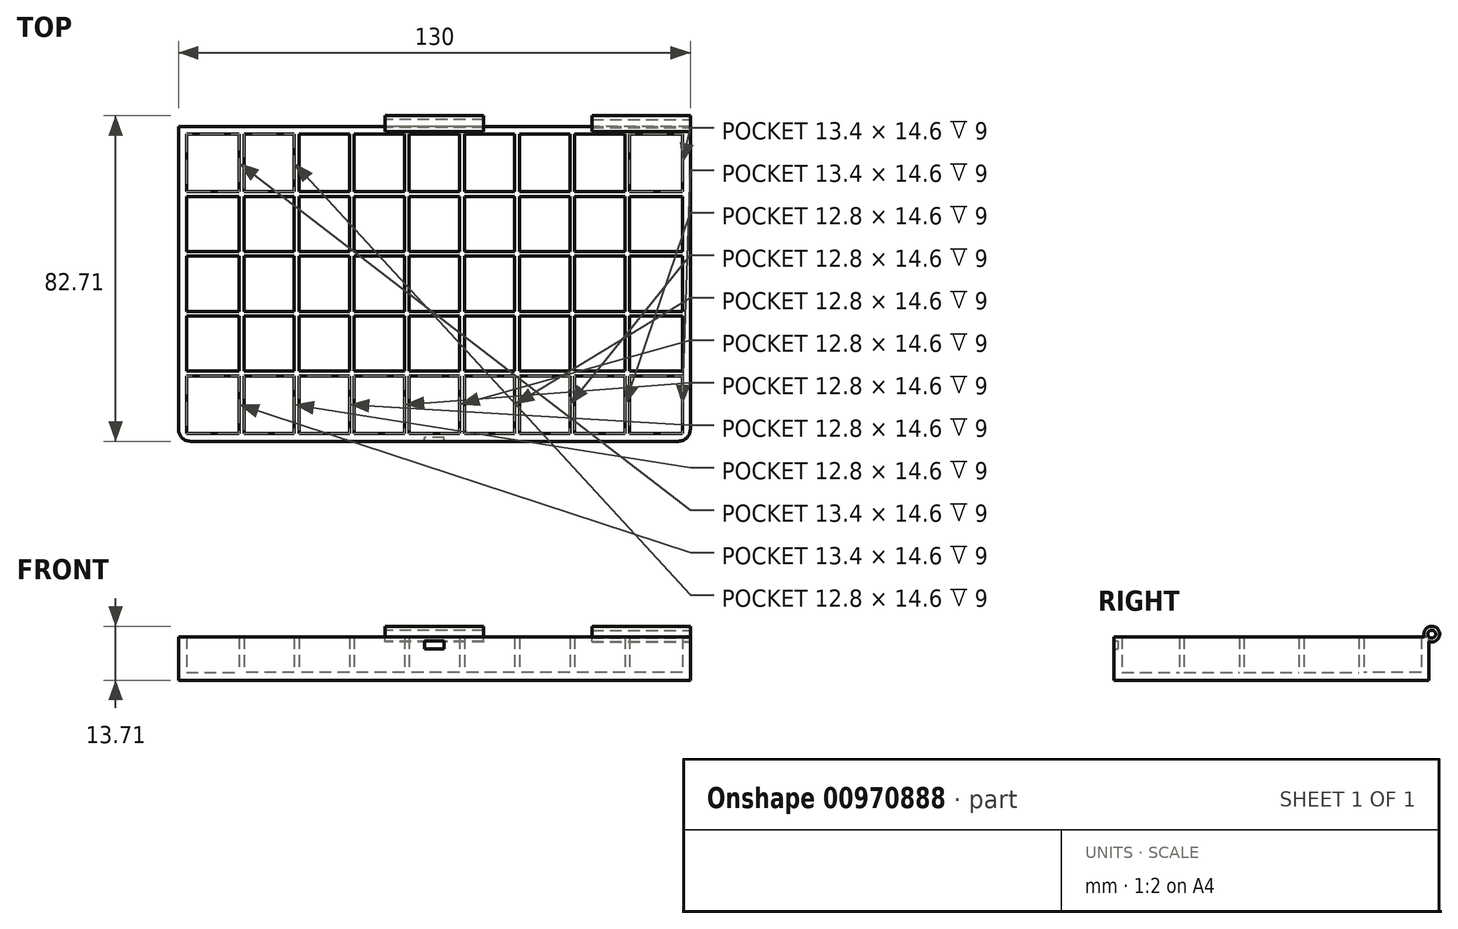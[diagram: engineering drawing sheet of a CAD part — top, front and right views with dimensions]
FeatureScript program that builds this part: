
annotation { "Feature Type Name" : "Feature", "Feature Type Description" : "" }
export const myFeature = defineFeature(function(context is Context, id is Id, definition is map)
    precondition{}
    {
        {
            var Q0;
            Q0=qCreatedBy(makeId("Top.planeOp"),FACE);
            var sketch = newSketch(context, id + "F0", { "sketchPlane" : qUnion([Q0])});
            skLineSegment(sketch, "E0.bottom", {"start": v(0, 0) * mm, "end": v(-130, 0) * mm});
            skLineSegment(sketch, "E0.top", {"start": v(0, 80) * mm, "end": v(-130, 80) * mm});
            skLineSegment(sketch, "E0.left", {"start": v(0, 0) * mm, "end": v(0, 80) * mm});
            skLineSegment(sketch, "E0.right", {"start": v(-130, 0) * mm, "end": v(-130, 80) * mm});
            skSolve(sketch);
        }
        {
            var Q0;
            Q0=makeQuery(id+"F0.imprint","IMPRINT",FACE,{"disambiguationData":[TD([[makeQuery(id+"F0.imprint","IMPRINT",EDGE,{"derivedFrom":sQuery(id+"F0.wireOp",EDGE,"E0.bottom")}),-1.0]])]});
            extrude(context, id + "F1", {"entities" : qUnion([Q0]), "depth" : 11 * mm, "offsetDistance" : 25 * mm});
        }
        {
            var Q0;
            Q0=makeQuery(id+"F1.opExtrude","CAP_FACE",FACE,{"disambiguationData":[OSD([sQuery(id+"F0.wireOp",EDGE,"E0.bottom"),sQuery(id+"F0.wireOp",EDGE,"E0.top"),sQuery(id+"F0.wireOp",EDGE,"E0.left"),sQuery(id+"F0.wireOp",EDGE,"E0.right")])],"isStart":false});
            shell(context, id + "F2", {"entities" : qUnion([Q0]), "thickness" : 2 * mm});
        }
        {
            var Q0;
            Q0=makeQuery(id+"F2.opShell","OFFSET_FACE",FACE,{"disambiguationData":[OSD([sQuery(id+"F0.wireOp",EDGE,"E0.bottom"),sQuery(id+"F0.wireOp",EDGE,"E0.top"),sQuery(id+"F0.wireOp",EDGE,"E0.left"),sQuery(id+"F0.wireOp",EDGE,"E0.right")])]});
            var sketch = newSketch(context, id + "F3", { "sketchPlane" : qUnion([Q0])});
            skLineSegment(sketch, "E1", {"start": v(-128, 62.8) * mm, "end": v(-2, 62.8) * mm, "construction": true});
            skLineSegment(sketch, "E2.0.1.0", {"start": v(-128, 47.6) * mm, "end": v(-2, 47.6) * mm, "construction": true});
            skLineSegment(sketch, "E2.0.2.0", {"start": v(-128, 32.4) * mm, "end": v(-2, 32.4) * mm, "construction": true});
            skLineSegment(sketch, "E2.0.3.0", {"start": v(-128, 17.2) * mm, "end": v(-2, 17.2) * mm, "construction": true});
            skLineSegment(sketch, "E2.direction1", {"start": v(-128, 62.8) * mm, "end": v(-103, 62.8) * mm, "construction": true});
            skLineSegment(sketch, "E2.direction2", {"start": v(-128, 62.8) * mm, "end": v(-128, 47.6) * mm, "construction": true});
            skLineSegment(sketch, "E3", {"start": v(-115.48, 78) * mm, "end": v(-115.48, 62.8) * mm, "construction": true});
            skLineSegment(sketch, "E4", {"start": v(-116.19, 17.2) * mm, "end": v(-116.19, 2) * mm, "construction": true});
            skLineSegment(sketch, "E5", {"start": v(-115.48, 62.8) * mm, "end": v(-115.48, 47.6) * mm, "construction": true});
            skLineSegment(sketch, "E6", {"start": v(-114, 78) * mm, "end": v(-114, 2) * mm, "construction": true});
            skLineSegment(sketch, "E7.1.0.0", {"start": v(-100, 78) * mm, "end": v(-100, 2) * mm, "construction": true});
            skLineSegment(sketch, "E7.2.0.0", {"start": v(-86, 78) * mm, "end": v(-86, 2) * mm, "construction": true});
            skLineSegment(sketch, "E7.3.0.0", {"start": v(-72, 78) * mm, "end": v(-72, 2) * mm, "construction": true});
            skLineSegment(sketch, "E7.4.0.0", {"start": v(-58, 78) * mm, "end": v(-58, 2) * mm, "construction": true});
            skLineSegment(sketch, "E7.5.0.0", {"start": v(-44, 78) * mm, "end": v(-44, 2) * mm, "construction": true});
            skLineSegment(sketch, "E7.6.0.0", {"start": v(-30, 78) * mm, "end": v(-30, 2) * mm, "construction": true});
            skLineSegment(sketch, "E7.7.0.0", {"start": v(-16, 78) * mm, "end": v(-16, 2) * mm, "construction": true});
            skLineSegment(sketch, "E7.direction1", {"start": v(-114, 2) * mm, "end": v(-100, 2) * mm, "construction": true});
            skLineSegment(sketch, "E8", {"start": v(-114, 25.91) * mm, "end": v(-128, 25.91) * mm, "construction": true});
            skLineSegment(sketch, "E9", {"start": v(-16, 25.73) * mm, "end": v(-2, 25.73) * mm, "construction": true});
            skLineSegment(sketch, "E10", {"start": v(-114, 25.91) * mm, "end": v(-100, 25.91) * mm, "construction": true});
            skArc(sketch, "E11.0.startCap", {"start": v(-128, 62.2) * mm, "mid": v(-128.6, 62.8) * mm, "end": v(-128, 63.4) * mm});
            skArc(sketch, "E11.0.endCap", {"start": v(-2, 63.4) * mm, "mid": v(-1.4, 62.8) * mm, "end": v(-2, 62.2) * mm});
            skLineSegment(sketch, "E11.0.left", {"start": v(-128, 63.4) * mm, "end": v(-2, 63.4) * mm});
            skLineSegment(sketch, "E11.0.right", {"start": v(-128, 62.2) * mm, "end": v(-2, 62.2) * mm});
            skArc(sketch, "E11.1.startCap", {"start": v(-30.6, 78) * mm, "mid": v(-30, 78.6) * mm, "end": v(-29.4, 78) * mm});
            skArc(sketch, "E11.1.endCap", {"start": v(-29.4, 2) * mm, "mid": v(-30, 1.4) * mm, "end": v(-30.6, 2) * mm});
            skLineSegment(sketch, "E11.1.left", {"start": v(-29.4, 78) * mm, "end": v(-29.4, 2) * mm});
            skLineSegment(sketch, "E11.1.right", {"start": v(-30.6, 78) * mm, "end": v(-30.6, 2) * mm});
            skArc(sketch, "E11.2.startCap", {"start": v(-86.6, 78) * mm, "mid": v(-86, 78.6) * mm, "end": v(-85.4, 78) * mm});
            skArc(sketch, "E11.2.endCap", {"start": v(-85.4, 2) * mm, "mid": v(-86, 1.4) * mm, "end": v(-86.6, 2) * mm});
            skLineSegment(sketch, "E11.2.left", {"start": v(-85.4, 78) * mm, "end": v(-85.4, 2) * mm});
            skLineSegment(sketch, "E11.2.right", {"start": v(-86.6, 78) * mm, "end": v(-86.6, 2) * mm});
            skArc(sketch, "E11.3.startCap", {"start": v(-100.6, 78) * mm, "mid": v(-100, 78.6) * mm, "end": v(-99.4, 78) * mm});
            skArc(sketch, "E11.3.endCap", {"start": v(-99.4, 2) * mm, "mid": v(-100, 1.4) * mm, "end": v(-100.6, 2) * mm});
            skLineSegment(sketch, "E11.3.left", {"start": v(-99.4, 78) * mm, "end": v(-99.4, 2) * mm});
            skLineSegment(sketch, "E11.3.right", {"start": v(-100.6, 78) * mm, "end": v(-100.6, 2) * mm});
            skArc(sketch, "E11.4.startCap", {"start": v(-44.6, 78) * mm, "mid": v(-44, 78.6) * mm, "end": v(-43.4, 78) * mm});
            skArc(sketch, "E11.4.endCap", {"start": v(-43.4, 2) * mm, "mid": v(-44, 1.4) * mm, "end": v(-44.6, 2) * mm});
            skLineSegment(sketch, "E11.4.left", {"start": v(-43.4, 78) * mm, "end": v(-43.4, 2) * mm});
            skLineSegment(sketch, "E11.4.right", {"start": v(-44.6, 78) * mm, "end": v(-44.6, 2) * mm});
            skArc(sketch, "E11.5.startCap", {"start": v(-128, 16.6) * mm, "mid": v(-128.6, 17.2) * mm, "end": v(-128, 17.8) * mm});
            skArc(sketch, "E11.5.endCap", {"start": v(-2, 17.8) * mm, "mid": v(-1.4, 17.2) * mm, "end": v(-2, 16.6) * mm});
            skLineSegment(sketch, "E11.5.left", {"start": v(-128, 17.8) * mm, "end": v(-2, 17.8) * mm});
            skLineSegment(sketch, "E11.5.right", {"start": v(-128, 16.6) * mm, "end": v(-2, 16.6) * mm});
            skArc(sketch, "E11.6.startCap", {"start": v(-128, 47) * mm, "mid": v(-128.6, 47.6) * mm, "end": v(-128, 48.2) * mm});
            skArc(sketch, "E11.6.endCap", {"start": v(-2, 48.2) * mm, "mid": v(-1.4, 47.6) * mm, "end": v(-2, 47) * mm});
            skLineSegment(sketch, "E11.6.left", {"start": v(-128, 48.2) * mm, "end": v(-2, 48.2) * mm});
            skLineSegment(sketch, "E11.6.right", {"start": v(-128, 47) * mm, "end": v(-2, 47) * mm});
            skArc(sketch, "E11.7.startCap", {"start": v(-114.6, 78) * mm, "mid": v(-114, 78.6) * mm, "end": v(-113.4, 78) * mm});
            skArc(sketch, "E11.7.endCap", {"start": v(-113.4, 2) * mm, "mid": v(-114, 1.4) * mm, "end": v(-114.6, 2) * mm});
            skLineSegment(sketch, "E11.7.left", {"start": v(-113.4, 78) * mm, "end": v(-113.4, 2) * mm});
            skLineSegment(sketch, "E11.7.right", {"start": v(-114.6, 78) * mm, "end": v(-114.6, 2) * mm});
            skArc(sketch, "E11.8.startCap", {"start": v(-16.6, 78) * mm, "mid": v(-16, 78.6) * mm, "end": v(-15.4, 78) * mm});
            skArc(sketch, "E11.8.endCap", {"start": v(-15.4, 2) * mm, "mid": v(-16, 1.4) * mm, "end": v(-16.6, 2) * mm});
            skLineSegment(sketch, "E11.8.left", {"start": v(-15.4, 78) * mm, "end": v(-15.4, 2) * mm});
            skLineSegment(sketch, "E11.8.right", {"start": v(-16.6, 78) * mm, "end": v(-16.6, 2) * mm});
            skArc(sketch, "E11.9.startCap", {"start": v(-58.6, 78) * mm, "mid": v(-58, 78.6) * mm, "end": v(-57.4, 78) * mm});
            skArc(sketch, "E11.9.endCap", {"start": v(-57.4, 2) * mm, "mid": v(-58, 1.4) * mm, "end": v(-58.6, 2) * mm});
            skLineSegment(sketch, "E11.9.left", {"start": v(-57.4, 78) * mm, "end": v(-57.4, 2) * mm});
            skLineSegment(sketch, "E11.9.right", {"start": v(-58.6, 78) * mm, "end": v(-58.6, 2) * mm});
            skArc(sketch, "E11.10.startCap", {"start": v(-72.6, 78) * mm, "mid": v(-72, 78.6) * mm, "end": v(-71.4, 78) * mm});
            skArc(sketch, "E11.10.endCap", {"start": v(-71.4, 2) * mm, "mid": v(-72, 1.4) * mm, "end": v(-72.6, 2) * mm});
            skLineSegment(sketch, "E11.10.left", {"start": v(-71.4, 78) * mm, "end": v(-71.4, 2) * mm});
            skLineSegment(sketch, "E11.10.right", {"start": v(-72.6, 78) * mm, "end": v(-72.6, 2) * mm});
            skArc(sketch, "E11.11.startCap", {"start": v(-128, 31.8) * mm, "mid": v(-128.6, 32.4) * mm, "end": v(-128, 33) * mm});
            skArc(sketch, "E11.11.endCap", {"start": v(-2, 33) * mm, "mid": v(-1.4, 32.4) * mm, "end": v(-2, 31.8) * mm});
            skLineSegment(sketch, "E11.11.left", {"start": v(-128, 33) * mm, "end": v(-2, 33) * mm});
            skLineSegment(sketch, "E11.11.right", {"start": v(-128, 31.8) * mm, "end": v(-2, 31.8) * mm});
            skSolve(sketch);
        }
        {
            var Q0;
            {var subQ0=sQuery(id+"F3.wireOp",EDGE,"E11.7.right");var subQ1=sQuery(id+"F3.wireOp",EDGE,"E11.0.left");var subQ2=makeQuery(id+"F3.imprint","INTERSECT",VERTEX,{"derivedFrom":[subQ1,subQ0]});Q0=makeQuery(id+"F3.imprint","IMPRINT",FACE,{"disambiguationData":[TD([[makeQuery(id+"F3.imprint","IMPRINT",EDGE,{"disambiguationData":[TD([[subQ2,-1.0]])],"derivedFrom":subQ1}),-1.0]])]});}
            var Q1;
            {var subQ0=sQuery(id+"F3.wireOp",EDGE,"E11.7.left");var subQ1=sQuery(id+"F3.wireOp",EDGE,"E11.0.left");var subQ2=makeQuery(id+"F3.imprint","INTERSECT",VERTEX,{"derivedFrom":[subQ1,subQ0]});Q1=makeQuery(id+"F3.imprint","IMPRINT",FACE,{"disambiguationData":[TD([[makeQuery(id+"F3.imprint","IMPRINT",EDGE,{"disambiguationData":[TD([[subQ2,-1.0]])],"derivedFrom":subQ1}),-1.0]])]});}
            var Q2;
            {var subQ0=sQuery(id+"F3.wireOp",EDGE,"E11.3.right");var subQ1=sQuery(id+"F3.wireOp",EDGE,"E11.0.left");var subQ2=makeQuery(id+"F3.imprint","INTERSECT",VERTEX,{"derivedFrom":[subQ1,subQ0]});Q2=makeQuery(id+"F3.imprint","IMPRINT",FACE,{"disambiguationData":[TD([[makeQuery(id+"F3.imprint","IMPRINT",EDGE,{"disambiguationData":[TD([[subQ2,-1.0]])],"derivedFrom":subQ1}),-1.0]])]});}
            var Q3;
            {var subQ0=sQuery(id+"F3.wireOp",EDGE,"E11.3.left");var subQ1=sQuery(id+"F3.wireOp",EDGE,"E11.0.left");var subQ2=makeQuery(id+"F3.imprint","INTERSECT",VERTEX,{"derivedFrom":[subQ1,subQ0]});Q3=makeQuery(id+"F3.imprint","IMPRINT",FACE,{"disambiguationData":[TD([[makeQuery(id+"F3.imprint","IMPRINT",EDGE,{"disambiguationData":[TD([[subQ2,-1.0]])],"derivedFrom":subQ1}),-1.0]])]});}
            var Q4;
            {var subQ0=sQuery(id+"F3.wireOp",EDGE,"E11.2.right");var subQ1=sQuery(id+"F3.wireOp",EDGE,"E11.0.left");var subQ2=makeQuery(id+"F3.imprint","INTERSECT",VERTEX,{"derivedFrom":[subQ1,subQ0]});Q4=makeQuery(id+"F3.imprint","IMPRINT",FACE,{"disambiguationData":[TD([[makeQuery(id+"F3.imprint","IMPRINT",EDGE,{"disambiguationData":[TD([[subQ2,-1.0]])],"derivedFrom":subQ1}),-1.0]])]});}
            var Q5;
            {var subQ0=sQuery(id+"F3.wireOp",EDGE,"E11.2.left");var subQ1=sQuery(id+"F3.wireOp",EDGE,"E11.0.left");var subQ2=makeQuery(id+"F3.imprint","INTERSECT",VERTEX,{"derivedFrom":[subQ1,subQ0]});Q5=makeQuery(id+"F3.imprint","IMPRINT",FACE,{"disambiguationData":[TD([[makeQuery(id+"F3.imprint","IMPRINT",EDGE,{"disambiguationData":[TD([[subQ2,-1.0]])],"derivedFrom":subQ1}),-1.0]])]});}
            var Q6;
            {var subQ0=sQuery(id+"F3.wireOp",EDGE,"E11.10.right");var subQ1=sQuery(id+"F3.wireOp",EDGE,"E11.0.left");var subQ2=makeQuery(id+"F3.imprint","INTERSECT",VERTEX,{"derivedFrom":[subQ1,subQ0]});Q6=makeQuery(id+"F3.imprint","IMPRINT",FACE,{"disambiguationData":[TD([[makeQuery(id+"F3.imprint","IMPRINT",EDGE,{"disambiguationData":[TD([[subQ2,-1.0]])],"derivedFrom":subQ1}),-1.0]])]});}
            var Q7;
            {var subQ0=sQuery(id+"F3.wireOp",EDGE,"E11.10.left");var subQ1=sQuery(id+"F3.wireOp",EDGE,"E11.0.left");var subQ2=makeQuery(id+"F3.imprint","INTERSECT",VERTEX,{"derivedFrom":[subQ1,subQ0]});Q7=makeQuery(id+"F3.imprint","IMPRINT",FACE,{"disambiguationData":[TD([[makeQuery(id+"F3.imprint","IMPRINT",EDGE,{"disambiguationData":[TD([[subQ2,-1.0]])],"derivedFrom":subQ1}),-1.0]])]});}
            var Q8;
            {var subQ0=sQuery(id+"F3.wireOp",EDGE,"E11.9.right");var subQ1=sQuery(id+"F3.wireOp",EDGE,"E11.0.left");var subQ2=makeQuery(id+"F3.imprint","INTERSECT",VERTEX,{"derivedFrom":[subQ1,subQ0]});Q8=makeQuery(id+"F3.imprint","IMPRINT",FACE,{"disambiguationData":[TD([[makeQuery(id+"F3.imprint","IMPRINT",EDGE,{"disambiguationData":[TD([[subQ2,-1.0]])],"derivedFrom":subQ1}),-1.0]])]});}
            var Q9;
            {var subQ0=sQuery(id+"F3.wireOp",EDGE,"E11.9.left");var subQ1=sQuery(id+"F3.wireOp",EDGE,"E11.0.left");var subQ2=makeQuery(id+"F3.imprint","INTERSECT",VERTEX,{"derivedFrom":[subQ1,subQ0]});Q9=makeQuery(id+"F3.imprint","IMPRINT",FACE,{"disambiguationData":[TD([[makeQuery(id+"F3.imprint","IMPRINT",EDGE,{"disambiguationData":[TD([[subQ2,-1.0]])],"derivedFrom":subQ1}),-1.0]])]});}
            var Q10;
            {var subQ0=sQuery(id+"F3.wireOp",EDGE,"E11.4.right");var subQ1=sQuery(id+"F3.wireOp",EDGE,"E11.0.left");var subQ2=makeQuery(id+"F3.imprint","INTERSECT",VERTEX,{"derivedFrom":[subQ1,subQ0]});Q10=makeQuery(id+"F3.imprint","IMPRINT",FACE,{"disambiguationData":[TD([[makeQuery(id+"F3.imprint","IMPRINT",EDGE,{"disambiguationData":[TD([[subQ2,-1.0]])],"derivedFrom":subQ1}),-1.0]])]});}
            var Q11;
            {var subQ0=sQuery(id+"F3.wireOp",EDGE,"E11.4.left");var subQ1=sQuery(id+"F3.wireOp",EDGE,"E11.0.left");var subQ2=makeQuery(id+"F3.imprint","INTERSECT",VERTEX,{"derivedFrom":[subQ1,subQ0]});Q11=makeQuery(id+"F3.imprint","IMPRINT",FACE,{"disambiguationData":[TD([[makeQuery(id+"F3.imprint","IMPRINT",EDGE,{"disambiguationData":[TD([[subQ2,-1.0]])],"derivedFrom":subQ1}),-1.0]])]});}
            var Q12;
            {var subQ0=sQuery(id+"F3.wireOp",EDGE,"E11.1.right");var subQ1=sQuery(id+"F3.wireOp",EDGE,"E11.0.left");var subQ2=makeQuery(id+"F3.imprint","INTERSECT",VERTEX,{"derivedFrom":[subQ1,subQ0]});Q12=makeQuery(id+"F3.imprint","IMPRINT",FACE,{"disambiguationData":[TD([[makeQuery(id+"F3.imprint","IMPRINT",EDGE,{"disambiguationData":[TD([[subQ2,-1.0]])],"derivedFrom":subQ1}),-1.0]])]});}
            var Q13;
            {var subQ0=sQuery(id+"F3.wireOp",EDGE,"E11.1.left");var subQ1=sQuery(id+"F3.wireOp",EDGE,"E11.0.left");var subQ2=makeQuery(id+"F3.imprint","INTERSECT",VERTEX,{"derivedFrom":[subQ1,subQ0]});Q13=makeQuery(id+"F3.imprint","IMPRINT",FACE,{"disambiguationData":[TD([[makeQuery(id+"F3.imprint","IMPRINT",EDGE,{"disambiguationData":[TD([[subQ2,-1.0]])],"derivedFrom":subQ1}),-1.0]])]});}
            var Q14;
            {var subQ0=sQuery(id+"F3.wireOp",EDGE,"E11.8.right");var subQ1=sQuery(id+"F3.wireOp",EDGE,"E11.0.left");var subQ2=makeQuery(id+"F3.imprint","INTERSECT",VERTEX,{"derivedFrom":[subQ1,subQ0]});Q14=makeQuery(id+"F3.imprint","IMPRINT",FACE,{"disambiguationData":[TD([[makeQuery(id+"F3.imprint","IMPRINT",EDGE,{"disambiguationData":[TD([[subQ2,-1.0]])],"derivedFrom":subQ1}),-1.0]])]});}
            var Q15;
            {var subQ0=sQuery(id+"F3.wireOp",EDGE,"E11.7.right");var subQ1=sQuery(id+"F3.wireOp",EDGE,"E11.0.right");var subQ2=makeQuery(id+"F3.imprint","INTERSECT",VERTEX,{"derivedFrom":[subQ1,subQ0]});Q15=makeQuery(id+"F3.imprint","IMPRINT",FACE,{"disambiguationData":[TD([[makeQuery(id+"F3.imprint","IMPRINT",EDGE,{"disambiguationData":[TD([[subQ2,-1.0]])],"derivedFrom":subQ1}),-1.0]])]});}
            var Q16;
            {var subQ0=sQuery(id+"F3.wireOp",EDGE,"E11.8.right");var subQ1=sQuery(id+"F3.wireOp",EDGE,"E11.0.right");var subQ2=makeQuery(id+"F3.imprint","INTERSECT",VERTEX,{"derivedFrom":[subQ1,subQ0]});Q16=makeQuery(id+"F3.imprint","IMPRINT",FACE,{"disambiguationData":[TD([[makeQuery(id+"F3.imprint","IMPRINT",EDGE,{"disambiguationData":[TD([[subQ2,-1.0]])],"derivedFrom":subQ1}),-1.0]])]});}
            var Q17;
            {var subQ0=sQuery(id+"F3.wireOp",EDGE,"E11.5.left");var subQ1=sQuery(id+"F3.wireOp",EDGE,"E11.1.left");var subQ2=makeQuery(id+"F3.imprint","INTERSECT",VERTEX,{"derivedFrom":[subQ1,subQ0]});Q17=makeQuery(id+"F3.imprint","IMPRINT",FACE,{"disambiguationData":[TD([[makeQuery(id+"F3.imprint","IMPRINT",EDGE,{"disambiguationData":[TD([[subQ2,-1.0]])],"derivedFrom":subQ1}),-1.0]])]});}
            var Q18;
            {var subQ0=sQuery(id+"F3.wireOp",EDGE,"E11.5.left");var subQ1=sQuery(id+"F3.wireOp",EDGE,"E11.1.left");var subQ2=makeQuery(id+"F3.imprint","INTERSECT",VERTEX,{"derivedFrom":[subQ1,subQ0]});Q18=makeQuery(id+"F3.imprint","IMPRINT",FACE,{"disambiguationData":[TD([[makeQuery(id+"F3.imprint","IMPRINT",EDGE,{"disambiguationData":[TD([[subQ2,-1.0]])],"derivedFrom":subQ1}),1.0]])]});}
            var Q19;
            {var subQ0=sQuery(id+"F3.wireOp",EDGE,"E11.5.left");var subQ1=sQuery(id+"F3.wireOp",EDGE,"E11.1.right");var subQ2=makeQuery(id+"F3.imprint","INTERSECT",VERTEX,{"derivedFrom":[subQ1,subQ0]});Q19=makeQuery(id+"F3.imprint","IMPRINT",FACE,{"disambiguationData":[TD([[makeQuery(id+"F3.imprint","IMPRINT",EDGE,{"disambiguationData":[TD([[subQ2,-1.0]])],"derivedFrom":subQ1}),-1.0]])]});}
            var Q20;
            {var subQ0=sQuery(id+"F3.wireOp",EDGE,"E11.5.left");var subQ1=sQuery(id+"F3.wireOp",EDGE,"E11.2.left");var subQ2=makeQuery(id+"F3.imprint","INTERSECT",VERTEX,{"derivedFrom":[subQ1,subQ0]});Q20=makeQuery(id+"F3.imprint","IMPRINT",FACE,{"disambiguationData":[TD([[makeQuery(id+"F3.imprint","IMPRINT",EDGE,{"disambiguationData":[TD([[subQ2,-1.0]])],"derivedFrom":subQ1}),-1.0]])]});}
            var Q21;
            {var subQ0=sQuery(id+"F3.wireOp",EDGE,"E11.5.left");var subQ1=sQuery(id+"F3.wireOp",EDGE,"E11.2.left");var subQ2=makeQuery(id+"F3.imprint","INTERSECT",VERTEX,{"derivedFrom":[subQ1,subQ0]});Q21=makeQuery(id+"F3.imprint","IMPRINT",FACE,{"disambiguationData":[TD([[makeQuery(id+"F3.imprint","IMPRINT",EDGE,{"disambiguationData":[TD([[subQ2,-1.0]])],"derivedFrom":subQ1}),1.0]])]});}
            var Q22;
            {var subQ0=sQuery(id+"F3.wireOp",EDGE,"E11.5.left");var subQ1=sQuery(id+"F3.wireOp",EDGE,"E11.2.right");var subQ2=makeQuery(id+"F3.imprint","INTERSECT",VERTEX,{"derivedFrom":[subQ1,subQ0]});Q22=makeQuery(id+"F3.imprint","IMPRINT",FACE,{"disambiguationData":[TD([[makeQuery(id+"F3.imprint","IMPRINT",EDGE,{"disambiguationData":[TD([[subQ2,-1.0]])],"derivedFrom":subQ1}),-1.0]])]});}
            var Q23;
            {var subQ0=sQuery(id+"F3.wireOp",EDGE,"E11.5.left");var subQ1=sQuery(id+"F3.wireOp",EDGE,"E11.3.left");var subQ2=makeQuery(id+"F3.imprint","INTERSECT",VERTEX,{"derivedFrom":[subQ1,subQ0]});Q23=makeQuery(id+"F3.imprint","IMPRINT",FACE,{"disambiguationData":[TD([[makeQuery(id+"F3.imprint","IMPRINT",EDGE,{"disambiguationData":[TD([[subQ2,-1.0]])],"derivedFrom":subQ1}),-1.0]])]});}
            var Q24;
            {var subQ0=sQuery(id+"F3.wireOp",EDGE,"E11.5.left");var subQ1=sQuery(id+"F3.wireOp",EDGE,"E11.3.right");var subQ2=makeQuery(id+"F3.imprint","INTERSECT",VERTEX,{"derivedFrom":[subQ1,subQ0]});Q24=makeQuery(id+"F3.imprint","IMPRINT",FACE,{"disambiguationData":[TD([[makeQuery(id+"F3.imprint","IMPRINT",EDGE,{"disambiguationData":[TD([[subQ2,-1.0]])],"derivedFrom":subQ1}),-1.0]])]});}
            var Q25;
            {var subQ0=sQuery(id+"F3.wireOp",EDGE,"E11.5.left");var subQ1=sQuery(id+"F3.wireOp",EDGE,"E11.4.left");var subQ2=makeQuery(id+"F3.imprint","INTERSECT",VERTEX,{"derivedFrom":[subQ1,subQ0]});Q25=makeQuery(id+"F3.imprint","IMPRINT",FACE,{"disambiguationData":[TD([[makeQuery(id+"F3.imprint","IMPRINT",EDGE,{"disambiguationData":[TD([[subQ2,-1.0]])],"derivedFrom":subQ1}),-1.0]])]});}
            var Q26;
            {var subQ0=sQuery(id+"F3.wireOp",EDGE,"E11.5.left");var subQ1=sQuery(id+"F3.wireOp",EDGE,"E11.4.right");var subQ2=makeQuery(id+"F3.imprint","INTERSECT",VERTEX,{"derivedFrom":[subQ1,subQ0]});Q26=makeQuery(id+"F3.imprint","IMPRINT",FACE,{"disambiguationData":[TD([[makeQuery(id+"F3.imprint","IMPRINT",EDGE,{"disambiguationData":[TD([[subQ2,-1.0]])],"derivedFrom":subQ1}),-1.0]])]});}
            var Q27;
            {var subQ0=sQuery(id+"F3.wireOp",EDGE,"E11.7.right");var subQ1=sQuery(id+"F3.wireOp",EDGE,"E11.5.left");var subQ2=makeQuery(id+"F3.imprint","INTERSECT",VERTEX,{"derivedFrom":[subQ1,subQ0]});Q27=makeQuery(id+"F3.imprint","IMPRINT",FACE,{"disambiguationData":[TD([[makeQuery(id+"F3.imprint","IMPRINT",EDGE,{"disambiguationData":[TD([[subQ2,-1.0]])],"derivedFrom":subQ1}),-1.0]])]});}
            var Q28;
            {var subQ0=sQuery(id+"F3.wireOp",EDGE,"E11.7.right");var subQ1=sQuery(id+"F3.wireOp",EDGE,"E11.5.left");var subQ2=makeQuery(id+"F3.imprint","INTERSECT",VERTEX,{"derivedFrom":[subQ1,subQ0]});Q28=makeQuery(id+"F3.imprint","IMPRINT",FACE,{"disambiguationData":[TD([[makeQuery(id+"F3.imprint","IMPRINT",EDGE,{"disambiguationData":[TD([[subQ2,-1.0]])],"derivedFrom":subQ1}),1.0]])]});}
            var Q29;
            {var subQ0=sQuery(id+"F3.wireOp",EDGE,"E11.10.right");var subQ1=sQuery(id+"F3.wireOp",EDGE,"E11.5.left");var subQ2=makeQuery(id+"F3.imprint","INTERSECT",VERTEX,{"derivedFrom":[subQ1,subQ0]});Q29=makeQuery(id+"F3.imprint","IMPRINT",FACE,{"disambiguationData":[TD([[makeQuery(id+"F3.imprint","IMPRINT",EDGE,{"disambiguationData":[TD([[subQ2,-1.0]])],"derivedFrom":subQ1}),-1.0]])]});}
            var Q30;
            {var subQ0=sQuery(id+"F3.wireOp",EDGE,"E11.10.left");var subQ1=sQuery(id+"F3.wireOp",EDGE,"E11.5.left");var subQ2=makeQuery(id+"F3.imprint","INTERSECT",VERTEX,{"derivedFrom":[subQ1,subQ0]});Q30=makeQuery(id+"F3.imprint","IMPRINT",FACE,{"disambiguationData":[TD([[makeQuery(id+"F3.imprint","IMPRINT",EDGE,{"disambiguationData":[TD([[subQ2,-1.0]])],"derivedFrom":subQ1}),-1.0]])]});}
            var Q31;
            {var subQ0=sQuery(id+"F3.wireOp",EDGE,"E11.9.right");var subQ1=sQuery(id+"F3.wireOp",EDGE,"E11.5.left");var subQ2=makeQuery(id+"F3.imprint","INTERSECT",VERTEX,{"derivedFrom":[subQ1,subQ0]});Q31=makeQuery(id+"F3.imprint","IMPRINT",FACE,{"disambiguationData":[TD([[makeQuery(id+"F3.imprint","IMPRINT",EDGE,{"disambiguationData":[TD([[subQ2,-1.0]])],"derivedFrom":subQ1}),-1.0]])]});}
            var Q32;
            {var subQ0=sQuery(id+"F3.wireOp",EDGE,"E11.8.right");var subQ1=sQuery(id+"F3.wireOp",EDGE,"E11.5.left");var subQ2=makeQuery(id+"F3.imprint","INTERSECT",VERTEX,{"derivedFrom":[subQ1,subQ0]});Q32=makeQuery(id+"F3.imprint","IMPRINT",FACE,{"disambiguationData":[TD([[makeQuery(id+"F3.imprint","IMPRINT",EDGE,{"disambiguationData":[TD([[subQ2,-1.0]])],"derivedFrom":subQ1}),-1.0]])]});}
            var Q33;
            {var subQ0=sQuery(id+"F3.wireOp",EDGE,"E11.8.right");var subQ1=sQuery(id+"F3.wireOp",EDGE,"E11.5.left");var subQ2=makeQuery(id+"F3.imprint","INTERSECT",VERTEX,{"derivedFrom":[subQ1,subQ0]});Q33=makeQuery(id+"F3.imprint","IMPRINT",FACE,{"disambiguationData":[TD([[makeQuery(id+"F3.imprint","IMPRINT",EDGE,{"disambiguationData":[TD([[subQ2,-1.0]])],"derivedFrom":subQ1}),1.0]])]});}
            var Q34;
            {var subQ0=sQuery(id+"F3.wireOp",EDGE,"E11.7.right");var subQ1=sQuery(id+"F3.wireOp",EDGE,"E11.6.left");var subQ2=makeQuery(id+"F3.imprint","INTERSECT",VERTEX,{"derivedFrom":[subQ1,subQ0]});Q34=makeQuery(id+"F3.imprint","IMPRINT",FACE,{"disambiguationData":[TD([[makeQuery(id+"F3.imprint","IMPRINT",EDGE,{"disambiguationData":[TD([[subQ2,-1.0]])],"derivedFrom":subQ1}),-1.0]])]});}
            var Q35;
            {var subQ0=sQuery(id+"F3.wireOp",EDGE,"E11.8.right");var subQ1=sQuery(id+"F3.wireOp",EDGE,"E11.6.left");var subQ2=makeQuery(id+"F3.imprint","INTERSECT",VERTEX,{"derivedFrom":[subQ1,subQ0]});Q35=makeQuery(id+"F3.imprint","IMPRINT",FACE,{"disambiguationData":[TD([[makeQuery(id+"F3.imprint","IMPRINT",EDGE,{"disambiguationData":[TD([[subQ2,-1.0]])],"derivedFrom":subQ1}),-1.0]])]});}
            var Q36;
            {var subQ0=sQuery(id+"F3.wireOp",EDGE,"E11.7.right");var subQ1=sQuery(id+"F3.wireOp",EDGE,"E11.6.right");var subQ2=makeQuery(id+"F3.imprint","INTERSECT",VERTEX,{"derivedFrom":[subQ1,subQ0]});Q36=makeQuery(id+"F3.imprint","IMPRINT",FACE,{"disambiguationData":[TD([[makeQuery(id+"F3.imprint","IMPRINT",EDGE,{"disambiguationData":[TD([[subQ2,-1.0]])],"derivedFrom":subQ1}),-1.0]])]});}
            var Q37;
            {var subQ0=sQuery(id+"F3.wireOp",EDGE,"E11.8.right");var subQ1=sQuery(id+"F3.wireOp",EDGE,"E11.6.right");var subQ2=makeQuery(id+"F3.imprint","INTERSECT",VERTEX,{"derivedFrom":[subQ1,subQ0]});Q37=makeQuery(id+"F3.imprint","IMPRINT",FACE,{"disambiguationData":[TD([[makeQuery(id+"F3.imprint","IMPRINT",EDGE,{"disambiguationData":[TD([[subQ2,-1.0]])],"derivedFrom":subQ1}),-1.0]])]});}
            var Q38;
            {var subQ0=sQuery(id+"F3.wireOp",EDGE,"E11.11.left");var subQ1=sQuery(id+"F3.wireOp",EDGE,"E11.7.left");var subQ2=makeQuery(id+"F3.imprint","INTERSECT",VERTEX,{"derivedFrom":[subQ1,subQ0]});Q38=makeQuery(id+"F3.imprint","IMPRINT",FACE,{"disambiguationData":[TD([[makeQuery(id+"F3.imprint","IMPRINT",EDGE,{"disambiguationData":[TD([[subQ2,-1.0]])],"derivedFrom":subQ1}),-1.0]])]});}
            var Q39;
            {var subQ0=sQuery(id+"F3.wireOp",EDGE,"E11.11.left");var subQ1=sQuery(id+"F3.wireOp",EDGE,"E11.8.left");var subQ2=makeQuery(id+"F3.imprint","INTERSECT",VERTEX,{"derivedFrom":[subQ1,subQ0]});Q39=makeQuery(id+"F3.imprint","IMPRINT",FACE,{"disambiguationData":[TD([[makeQuery(id+"F3.imprint","IMPRINT",EDGE,{"disambiguationData":[TD([[subQ2,-1.0]])],"derivedFrom":subQ1}),-1.0]])]});}
            var Q40;
            {var subQ0=sQuery(id+"F3.wireOp",EDGE,"E11.0.startCap");Q40=makeQuery(id+"F3.imprint","IMPRINT",FACE,{"disambiguationData":[TD([[makeQuery(id+"F3.imprint","IMPRINT",EDGE,{"derivedFrom":subQ0}),-1.0]])]});}
            var Q41;
            {var subQ0=sQuery(id+"F3.wireOp",EDGE,"E11.0.endCap");Q41=makeQuery(id+"F3.imprint","IMPRINT",FACE,{"disambiguationData":[TD([[makeQuery(id+"F3.imprint","IMPRINT",EDGE,{"derivedFrom":subQ0}),-1.0]])]});}
            var Q42;
            {var subQ0=sQuery(id+"F3.wireOp",EDGE,"E11.1.startCap");Q42=makeQuery(id+"F3.imprint","IMPRINT",FACE,{"disambiguationData":[TD([[makeQuery(id+"F3.imprint","IMPRINT",EDGE,{"derivedFrom":subQ0}),-1.0]])]});}
            var Q43;
            {var subQ0=sQuery(id+"F3.wireOp",EDGE,"E11.1.endCap");Q43=makeQuery(id+"F3.imprint","IMPRINT",FACE,{"disambiguationData":[TD([[makeQuery(id+"F3.imprint","IMPRINT",EDGE,{"derivedFrom":subQ0}),-1.0]])]});}
            var Q44;
            {var subQ0=sQuery(id+"F3.wireOp",EDGE,"E11.2.startCap");Q44=makeQuery(id+"F3.imprint","IMPRINT",FACE,{"disambiguationData":[TD([[makeQuery(id+"F3.imprint","IMPRINT",EDGE,{"derivedFrom":subQ0}),-1.0]])]});}
            var Q45;
            {var subQ0=sQuery(id+"F3.wireOp",EDGE,"E11.2.endCap");Q45=makeQuery(id+"F3.imprint","IMPRINT",FACE,{"disambiguationData":[TD([[makeQuery(id+"F3.imprint","IMPRINT",EDGE,{"derivedFrom":subQ0}),-1.0]])]});}
            var Q46;
            {var subQ0=sQuery(id+"F3.wireOp",EDGE,"E11.3.startCap");Q46=makeQuery(id+"F3.imprint","IMPRINT",FACE,{"disambiguationData":[TD([[makeQuery(id+"F3.imprint","IMPRINT",EDGE,{"derivedFrom":subQ0}),-1.0]])]});}
            var Q47;
            {var subQ0=sQuery(id+"F3.wireOp",EDGE,"E11.3.endCap");Q47=makeQuery(id+"F3.imprint","IMPRINT",FACE,{"disambiguationData":[TD([[makeQuery(id+"F3.imprint","IMPRINT",EDGE,{"derivedFrom":subQ0}),-1.0]])]});}
            var Q48;
            {var subQ0=sQuery(id+"F3.wireOp",EDGE,"E11.4.startCap");Q48=makeQuery(id+"F3.imprint","IMPRINT",FACE,{"disambiguationData":[TD([[makeQuery(id+"F3.imprint","IMPRINT",EDGE,{"derivedFrom":subQ0}),-1.0]])]});}
            var Q49;
            {var subQ0=sQuery(id+"F3.wireOp",EDGE,"E11.4.endCap");Q49=makeQuery(id+"F3.imprint","IMPRINT",FACE,{"disambiguationData":[TD([[makeQuery(id+"F3.imprint","IMPRINT",EDGE,{"derivedFrom":subQ0}),-1.0]])]});}
            var Q50;
            {var subQ0=sQuery(id+"F3.wireOp",EDGE,"E11.5.startCap");Q50=makeQuery(id+"F3.imprint","IMPRINT",FACE,{"disambiguationData":[TD([[makeQuery(id+"F3.imprint","IMPRINT",EDGE,{"derivedFrom":subQ0}),-1.0]])]});}
            var Q51;
            {var subQ0=sQuery(id+"F3.wireOp",EDGE,"E11.5.endCap");Q51=makeQuery(id+"F3.imprint","IMPRINT",FACE,{"disambiguationData":[TD([[makeQuery(id+"F3.imprint","IMPRINT",EDGE,{"derivedFrom":subQ0}),-1.0]])]});}
            var Q52;
            {var subQ0=sQuery(id+"F3.wireOp",EDGE,"E11.6.startCap");Q52=makeQuery(id+"F3.imprint","IMPRINT",FACE,{"disambiguationData":[TD([[makeQuery(id+"F3.imprint","IMPRINT",EDGE,{"derivedFrom":subQ0}),-1.0]])]});}
            var Q53;
            {var subQ0=sQuery(id+"F3.wireOp",EDGE,"E11.6.endCap");Q53=makeQuery(id+"F3.imprint","IMPRINT",FACE,{"disambiguationData":[TD([[makeQuery(id+"F3.imprint","IMPRINT",EDGE,{"derivedFrom":subQ0}),-1.0]])]});}
            var Q54;
            {var subQ0=sQuery(id+"F3.wireOp",EDGE,"E11.7.startCap");Q54=makeQuery(id+"F3.imprint","IMPRINT",FACE,{"disambiguationData":[TD([[makeQuery(id+"F3.imprint","IMPRINT",EDGE,{"derivedFrom":subQ0}),-1.0]])]});}
            var Q55;
            {var subQ0=sQuery(id+"F3.wireOp",EDGE,"E11.7.endCap");Q55=makeQuery(id+"F3.imprint","IMPRINT",FACE,{"disambiguationData":[TD([[makeQuery(id+"F3.imprint","IMPRINT",EDGE,{"derivedFrom":subQ0}),-1.0]])]});}
            var Q56;
            {var subQ0=sQuery(id+"F3.wireOp",EDGE,"E11.8.startCap");Q56=makeQuery(id+"F3.imprint","IMPRINT",FACE,{"disambiguationData":[TD([[makeQuery(id+"F3.imprint","IMPRINT",EDGE,{"derivedFrom":subQ0}),-1.0]])]});}
            var Q57;
            {var subQ0=sQuery(id+"F3.wireOp",EDGE,"E11.8.endCap");Q57=makeQuery(id+"F3.imprint","IMPRINT",FACE,{"disambiguationData":[TD([[makeQuery(id+"F3.imprint","IMPRINT",EDGE,{"derivedFrom":subQ0}),-1.0]])]});}
            var Q58;
            {var subQ0=sQuery(id+"F3.wireOp",EDGE,"E11.9.startCap");Q58=makeQuery(id+"F3.imprint","IMPRINT",FACE,{"disambiguationData":[TD([[makeQuery(id+"F3.imprint","IMPRINT",EDGE,{"derivedFrom":subQ0}),-1.0]])]});}
            var Q59;
            {var subQ0=sQuery(id+"F3.wireOp",EDGE,"E11.9.endCap");Q59=makeQuery(id+"F3.imprint","IMPRINT",FACE,{"disambiguationData":[TD([[makeQuery(id+"F3.imprint","IMPRINT",EDGE,{"derivedFrom":subQ0}),-1.0]])]});}
            var Q60;
            {var subQ0=sQuery(id+"F3.wireOp",EDGE,"E11.10.startCap");Q60=makeQuery(id+"F3.imprint","IMPRINT",FACE,{"disambiguationData":[TD([[makeQuery(id+"F3.imprint","IMPRINT",EDGE,{"derivedFrom":subQ0}),-1.0]])]});}
            var Q61;
            {var subQ0=sQuery(id+"F3.wireOp",EDGE,"E11.10.endCap");Q61=makeQuery(id+"F3.imprint","IMPRINT",FACE,{"disambiguationData":[TD([[makeQuery(id+"F3.imprint","IMPRINT",EDGE,{"derivedFrom":subQ0}),-1.0]])]});}
            var Q62;
            {var subQ0=sQuery(id+"F3.wireOp",EDGE,"E11.11.startCap");Q62=makeQuery(id+"F3.imprint","IMPRINT",FACE,{"disambiguationData":[TD([[makeQuery(id+"F3.imprint","IMPRINT",EDGE,{"derivedFrom":subQ0}),-1.0]])]});}
            var Q63;
            {var subQ0=sQuery(id+"F3.wireOp",EDGE,"E11.11.endCap");Q63=makeQuery(id+"F3.imprint","IMPRINT",FACE,{"disambiguationData":[TD([[makeQuery(id+"F3.imprint","IMPRINT",EDGE,{"derivedFrom":subQ0}),-1.0]])]});}
            var Q64;
            {var subQ0=sQuery(id+"F3.wireOp",EDGE,"E11.0.left");var subQ5=sQuery(id+"F3.wireOp",EDGE,"E11.7.right");var subQ6=makeQuery(id+"F3.imprint","INTERSECT",VERTEX,{"derivedFrom":[subQ0,subQ5]});Q64=makeQuery(id+"F3.imprint","IMPRINT",FACE,{"disambiguationData":[TD([[makeQuery(id+"F3.imprint","IMPRINT",EDGE,{"disambiguationData":[TD([[subQ6,-1.0]])],"derivedFrom":subQ5}),-1.0]])]});}
            var Q65;
            {var subQ0=sQuery(id+"F3.wireOp",EDGE,"E11.7.right");var subQ1=sQuery(id+"F3.wireOp",EDGE,"E11.0.left");var subQ2=makeQuery(id+"F3.imprint","INTERSECT",VERTEX,{"derivedFrom":[subQ1,subQ0]});Q65=makeQuery(id+"F3.imprint","IMPRINT",FACE,{"disambiguationData":[TD([[makeQuery(id+"F3.imprint","IMPRINT",EDGE,{"disambiguationData":[TD([[subQ2,-1.0]])],"derivedFrom":subQ1}),1.0]])]});}
            var Q66;
            {var subQ0=sQuery(id+"F3.wireOp",EDGE,"E11.3.right");var subQ1=sQuery(id+"F3.wireOp",EDGE,"E11.0.left");var subQ2=makeQuery(id+"F3.imprint","INTERSECT",VERTEX,{"derivedFrom":[subQ1,subQ0]});Q66=makeQuery(id+"F3.imprint","IMPRINT",FACE,{"disambiguationData":[TD([[makeQuery(id+"F3.imprint","IMPRINT",EDGE,{"disambiguationData":[TD([[subQ2,-1.0]])],"derivedFrom":subQ1}),1.0]])]});}
            var Q67;
            {var subQ0=sQuery(id+"F3.wireOp",EDGE,"E11.2.right");var subQ1=sQuery(id+"F3.wireOp",EDGE,"E11.0.left");var subQ2=makeQuery(id+"F3.imprint","INTERSECT",VERTEX,{"derivedFrom":[subQ1,subQ0]});Q67=makeQuery(id+"F3.imprint","IMPRINT",FACE,{"disambiguationData":[TD([[makeQuery(id+"F3.imprint","IMPRINT",EDGE,{"disambiguationData":[TD([[subQ2,-1.0]])],"derivedFrom":subQ1}),1.0]])]});}
            var Q68;
            {var subQ0=sQuery(id+"F3.wireOp",EDGE,"E11.10.right");var subQ1=sQuery(id+"F3.wireOp",EDGE,"E11.0.left");var subQ2=makeQuery(id+"F3.imprint","INTERSECT",VERTEX,{"derivedFrom":[subQ1,subQ0]});Q68=makeQuery(id+"F3.imprint","IMPRINT",FACE,{"disambiguationData":[TD([[makeQuery(id+"F3.imprint","IMPRINT",EDGE,{"disambiguationData":[TD([[subQ2,-1.0]])],"derivedFrom":subQ1}),1.0]])]});}
            var Q69;
            {var subQ0=sQuery(id+"F3.wireOp",EDGE,"E11.9.right");var subQ1=sQuery(id+"F3.wireOp",EDGE,"E11.0.left");var subQ2=makeQuery(id+"F3.imprint","INTERSECT",VERTEX,{"derivedFrom":[subQ1,subQ0]});Q69=makeQuery(id+"F3.imprint","IMPRINT",FACE,{"disambiguationData":[TD([[makeQuery(id+"F3.imprint","IMPRINT",EDGE,{"disambiguationData":[TD([[subQ2,-1.0]])],"derivedFrom":subQ1}),1.0]])]});}
            var Q70;
            {var subQ0=sQuery(id+"F3.wireOp",EDGE,"E11.4.right");var subQ1=sQuery(id+"F3.wireOp",EDGE,"E11.0.left");var subQ2=makeQuery(id+"F3.imprint","INTERSECT",VERTEX,{"derivedFrom":[subQ1,subQ0]});Q70=makeQuery(id+"F3.imprint","IMPRINT",FACE,{"disambiguationData":[TD([[makeQuery(id+"F3.imprint","IMPRINT",EDGE,{"disambiguationData":[TD([[subQ2,-1.0]])],"derivedFrom":subQ1}),1.0]])]});}
            var Q71;
            {var subQ0=sQuery(id+"F3.wireOp",EDGE,"E11.1.right");var subQ1=sQuery(id+"F3.wireOp",EDGE,"E11.0.left");var subQ2=makeQuery(id+"F3.imprint","INTERSECT",VERTEX,{"derivedFrom":[subQ1,subQ0]});Q71=makeQuery(id+"F3.imprint","IMPRINT",FACE,{"disambiguationData":[TD([[makeQuery(id+"F3.imprint","IMPRINT",EDGE,{"disambiguationData":[TD([[subQ2,-1.0]])],"derivedFrom":subQ1}),1.0]])]});}
            var Q72;
            {var subQ0=sQuery(id+"F3.wireOp",EDGE,"E11.8.right");var subQ1=sQuery(id+"F3.wireOp",EDGE,"E11.0.left");var subQ2=makeQuery(id+"F3.imprint","INTERSECT",VERTEX,{"derivedFrom":[subQ1,subQ0]});Q72=makeQuery(id+"F3.imprint","IMPRINT",FACE,{"disambiguationData":[TD([[makeQuery(id+"F3.imprint","IMPRINT",EDGE,{"disambiguationData":[TD([[subQ2,-1.0]])],"derivedFrom":subQ1}),1.0]])]});}
            var Q73;
            {var subQ0=sQuery(id+"F3.wireOp",EDGE,"E11.0.left");var subQ5=sQuery(id+"F3.wireOp",EDGE,"E11.8.left");var subQ6=makeQuery(id+"F3.imprint","INTERSECT",VERTEX,{"derivedFrom":[subQ0,subQ5]});Q73=makeQuery(id+"F3.imprint","IMPRINT",FACE,{"disambiguationData":[TD([[makeQuery(id+"F3.imprint","IMPRINT",EDGE,{"disambiguationData":[TD([[subQ6,-1.0]])],"derivedFrom":subQ5}),1.0]])]});}
            var Q74;
            {var subQ0=sQuery(id+"F3.wireOp",EDGE,"E11.1.left");var subQ5=sQuery(id+"F3.wireOp",EDGE,"E11.5.right");var subQ6=makeQuery(id+"F3.imprint","INTERSECT",VERTEX,{"derivedFrom":[subQ0,subQ5]});Q74=makeQuery(id+"F3.imprint","IMPRINT",FACE,{"disambiguationData":[TD([[makeQuery(id+"F3.imprint","IMPRINT",EDGE,{"disambiguationData":[TD([[subQ6,1.0]])],"derivedFrom":subQ5}),-1.0]])]});}
            var Q75;
            {var subQ0=sQuery(id+"F3.wireOp",EDGE,"E11.2.left");var subQ5=sQuery(id+"F3.wireOp",EDGE,"E11.5.right");var subQ6=makeQuery(id+"F3.imprint","INTERSECT",VERTEX,{"derivedFrom":[subQ0,subQ5]});Q75=makeQuery(id+"F3.imprint","IMPRINT",FACE,{"disambiguationData":[TD([[makeQuery(id+"F3.imprint","IMPRINT",EDGE,{"disambiguationData":[TD([[subQ6,1.0]])],"derivedFrom":subQ5}),-1.0]])]});}
            var Q76;
            {var subQ0=sQuery(id+"F3.wireOp",EDGE,"E11.3.left");var subQ5=sQuery(id+"F3.wireOp",EDGE,"E11.5.right");var subQ6=makeQuery(id+"F3.imprint","INTERSECT",VERTEX,{"derivedFrom":[subQ0,subQ5]});Q76=makeQuery(id+"F3.imprint","IMPRINT",FACE,{"disambiguationData":[TD([[makeQuery(id+"F3.imprint","IMPRINT",EDGE,{"disambiguationData":[TD([[subQ6,1.0]])],"derivedFrom":subQ5}),-1.0]])]});}
            var Q77;
            {var subQ0=sQuery(id+"F3.wireOp",EDGE,"E11.4.left");var subQ5=sQuery(id+"F3.wireOp",EDGE,"E11.5.right");var subQ6=makeQuery(id+"F3.imprint","INTERSECT",VERTEX,{"derivedFrom":[subQ0,subQ5]});Q77=makeQuery(id+"F3.imprint","IMPRINT",FACE,{"disambiguationData":[TD([[makeQuery(id+"F3.imprint","IMPRINT",EDGE,{"disambiguationData":[TD([[subQ6,1.0]])],"derivedFrom":subQ5}),-1.0]])]});}
            var Q78;
            {var subQ0=sQuery(id+"F3.wireOp",EDGE,"E11.5.left");var subQ5=sQuery(id+"F3.wireOp",EDGE,"E11.7.right");var subQ6=makeQuery(id+"F3.imprint","INTERSECT",VERTEX,{"derivedFrom":[subQ0,subQ5]});Q78=makeQuery(id+"F3.imprint","IMPRINT",FACE,{"disambiguationData":[TD([[makeQuery(id+"F3.imprint","IMPRINT",EDGE,{"disambiguationData":[TD([[subQ6,-1.0]])],"derivedFrom":subQ5}),-1.0]])]});}
            var Q79;
            {var subQ0=sQuery(id+"F3.wireOp",EDGE,"E11.5.left");var subQ5=sQuery(id+"F3.wireOp",EDGE,"E11.8.left");var subQ6=makeQuery(id+"F3.imprint","INTERSECT",VERTEX,{"derivedFrom":[subQ0,subQ5]});Q79=makeQuery(id+"F3.imprint","IMPRINT",FACE,{"disambiguationData":[TD([[makeQuery(id+"F3.imprint","IMPRINT",EDGE,{"disambiguationData":[TD([[subQ6,-1.0]])],"derivedFrom":subQ5}),1.0]])]});}
            var Q80;
            {var subQ0=sQuery(id+"F3.wireOp",EDGE,"E11.7.right");var subQ1=sQuery(id+"F3.wireOp",EDGE,"E11.5.right");var subQ2=makeQuery(id+"F3.imprint","INTERSECT",VERTEX,{"derivedFrom":[subQ1,subQ0]});Q80=makeQuery(id+"F3.imprint","IMPRINT",FACE,{"disambiguationData":[TD([[makeQuery(id+"F3.imprint","IMPRINT",EDGE,{"disambiguationData":[TD([[subQ2,-1.0]])],"derivedFrom":subQ1}),-1.0]])]});}
            var Q81;
            {var subQ0=sQuery(id+"F3.wireOp",EDGE,"E11.10.right");var subQ1=sQuery(id+"F3.wireOp",EDGE,"E11.5.right");var subQ2=makeQuery(id+"F3.imprint","INTERSECT",VERTEX,{"derivedFrom":[subQ1,subQ0]});Q81=makeQuery(id+"F3.imprint","IMPRINT",FACE,{"disambiguationData":[TD([[makeQuery(id+"F3.imprint","IMPRINT",EDGE,{"disambiguationData":[TD([[subQ2,-1.0]])],"derivedFrom":subQ1}),-1.0]])]});}
            var Q82;
            {var subQ0=sQuery(id+"F3.wireOp",EDGE,"E11.9.right");var subQ1=sQuery(id+"F3.wireOp",EDGE,"E11.5.right");var subQ2=makeQuery(id+"F3.imprint","INTERSECT",VERTEX,{"derivedFrom":[subQ1,subQ0]});Q82=makeQuery(id+"F3.imprint","IMPRINT",FACE,{"disambiguationData":[TD([[makeQuery(id+"F3.imprint","IMPRINT",EDGE,{"disambiguationData":[TD([[subQ2,-1.0]])],"derivedFrom":subQ1}),-1.0]])]});}
            var Q83;
            {var subQ0=sQuery(id+"F3.wireOp",EDGE,"E11.8.right");var subQ1=sQuery(id+"F3.wireOp",EDGE,"E11.5.right");var subQ2=makeQuery(id+"F3.imprint","INTERSECT",VERTEX,{"derivedFrom":[subQ1,subQ0]});Q83=makeQuery(id+"F3.imprint","IMPRINT",FACE,{"disambiguationData":[TD([[makeQuery(id+"F3.imprint","IMPRINT",EDGE,{"disambiguationData":[TD([[subQ2,-1.0]])],"derivedFrom":subQ1}),-1.0]])]});}
            var Q84;
            {var subQ0=sQuery(id+"F3.wireOp",EDGE,"E11.6.left");var subQ5=sQuery(id+"F3.wireOp",EDGE,"E11.7.right");var subQ6=makeQuery(id+"F3.imprint","INTERSECT",VERTEX,{"derivedFrom":[subQ0,subQ5]});Q84=makeQuery(id+"F3.imprint","IMPRINT",FACE,{"disambiguationData":[TD([[makeQuery(id+"F3.imprint","IMPRINT",EDGE,{"disambiguationData":[TD([[subQ6,-1.0]])],"derivedFrom":subQ5}),-1.0]])]});}
            var Q85;
            {var subQ0=sQuery(id+"F3.wireOp",EDGE,"E11.6.left");var subQ5=sQuery(id+"F3.wireOp",EDGE,"E11.8.left");var subQ6=makeQuery(id+"F3.imprint","INTERSECT",VERTEX,{"derivedFrom":[subQ0,subQ5]});Q85=makeQuery(id+"F3.imprint","IMPRINT",FACE,{"disambiguationData":[TD([[makeQuery(id+"F3.imprint","IMPRINT",EDGE,{"disambiguationData":[TD([[subQ6,-1.0]])],"derivedFrom":subQ5}),1.0]])]});}
            var Q86;
            {var subQ0=sQuery(id+"F3.wireOp",EDGE,"E11.11.left");var subQ1=sQuery(id+"F3.wireOp",EDGE,"E11.7.right");var subQ2=makeQuery(id+"F3.imprint","INTERSECT",VERTEX,{"derivedFrom":[subQ1,subQ0]});Q86=makeQuery(id+"F3.imprint","IMPRINT",FACE,{"disambiguationData":[TD([[makeQuery(id+"F3.imprint","IMPRINT",EDGE,{"disambiguationData":[TD([[subQ2,-1.0]])],"derivedFrom":subQ1}),-1.0]])]});}
            var Q87;
            {var subQ0=sQuery(id+"F3.wireOp",EDGE,"E11.11.left");var subQ1=sQuery(id+"F3.wireOp",EDGE,"E11.8.left");var subQ2=makeQuery(id+"F3.imprint","INTERSECT",VERTEX,{"derivedFrom":[subQ1,subQ0]});Q87=makeQuery(id+"F3.imprint","IMPRINT",FACE,{"disambiguationData":[TD([[makeQuery(id+"F3.imprint","IMPRINT",EDGE,{"disambiguationData":[TD([[subQ2,-1.0]])],"derivedFrom":subQ1}),1.0]])]});}
            var Q88;
            {var subQ0=sQuery(id+"F3.wireOp",EDGE,"E11.3.right");var subQ1=sQuery(id+"F3.wireOp",EDGE,"E11.0.right");var subQ2=makeQuery(id+"F3.imprint","INTERSECT",VERTEX,{"derivedFrom":[subQ1,subQ0]});Q88=makeQuery(id+"F3.imprint","IMPRINT",FACE,{"disambiguationData":[TD([[makeQuery(id+"F3.imprint","IMPRINT",EDGE,{"disambiguationData":[TD([[subQ2,-1.0]])],"derivedFrom":subQ1}),-1.0]])]});}
            var Q89;
            {var subQ0=sQuery(id+"F3.wireOp",EDGE,"E11.6.left");var subQ1=sQuery(id+"F3.wireOp",EDGE,"E11.3.right");var subQ2=makeQuery(id+"F3.imprint","INTERSECT",VERTEX,{"derivedFrom":[subQ1,subQ0]});Q89=makeQuery(id+"F3.imprint","IMPRINT",FACE,{"disambiguationData":[TD([[makeQuery(id+"F3.imprint","IMPRINT",EDGE,{"disambiguationData":[TD([[subQ2,-1.0]])],"derivedFrom":subQ1}),-1.0]])]});}
            var Q90;
            {var subQ0=sQuery(id+"F3.wireOp",EDGE,"E11.6.left");var subQ1=sQuery(id+"F3.wireOp",EDGE,"E11.3.left");var subQ2=makeQuery(id+"F3.imprint","INTERSECT",VERTEX,{"derivedFrom":[subQ1,subQ0]});Q90=makeQuery(id+"F3.imprint","IMPRINT",FACE,{"disambiguationData":[TD([[makeQuery(id+"F3.imprint","IMPRINT",EDGE,{"disambiguationData":[TD([[subQ2,-1.0]])],"derivedFrom":subQ1}),-1.0]])]});}
            var Q91;
            {var subQ0=sQuery(id+"F3.wireOp",EDGE,"E11.6.left");var subQ1=sQuery(id+"F3.wireOp",EDGE,"E11.2.right");var subQ2=makeQuery(id+"F3.imprint","INTERSECT",VERTEX,{"derivedFrom":[subQ1,subQ0]});Q91=makeQuery(id+"F3.imprint","IMPRINT",FACE,{"disambiguationData":[TD([[makeQuery(id+"F3.imprint","IMPRINT",EDGE,{"disambiguationData":[TD([[subQ2,-1.0]])],"derivedFrom":subQ1}),-1.0]])]});}
            var Q92;
            {var subQ0=sQuery(id+"F3.wireOp",EDGE,"E11.6.right");var subQ1=sQuery(id+"F3.wireOp",EDGE,"E11.3.left");var subQ2=makeQuery(id+"F3.imprint","INTERSECT",VERTEX,{"derivedFrom":[subQ1,subQ0]});Q92=makeQuery(id+"F3.imprint","IMPRINT",FACE,{"disambiguationData":[TD([[makeQuery(id+"F3.imprint","IMPRINT",EDGE,{"disambiguationData":[TD([[subQ2,-1.0]])],"derivedFrom":subQ1}),-1.0]])]});}
            var Q93;
            {var subQ0=sQuery(id+"F3.wireOp",EDGE,"E11.6.left");var subQ1=sQuery(id+"F3.wireOp",EDGE,"E11.2.left");var subQ2=makeQuery(id+"F3.imprint","INTERSECT",VERTEX,{"derivedFrom":[subQ1,subQ0]});Q93=makeQuery(id+"F3.imprint","IMPRINT",FACE,{"disambiguationData":[TD([[makeQuery(id+"F3.imprint","IMPRINT",EDGE,{"disambiguationData":[TD([[subQ2,-1.0]])],"derivedFrom":subQ1}),-1.0]])]});}
            var Q94;
            {var subQ0=sQuery(id+"F3.wireOp",EDGE,"E11.2.right");var subQ1=sQuery(id+"F3.wireOp",EDGE,"E11.0.right");var subQ2=makeQuery(id+"F3.imprint","INTERSECT",VERTEX,{"derivedFrom":[subQ1,subQ0]});Q94=makeQuery(id+"F3.imprint","IMPRINT",FACE,{"disambiguationData":[TD([[makeQuery(id+"F3.imprint","IMPRINT",EDGE,{"disambiguationData":[TD([[subQ2,-1.0]])],"derivedFrom":subQ1}),-1.0]])]});}
            var Q95;
            {var subQ0=sQuery(id+"F3.wireOp",EDGE,"E11.10.right");var subQ1=sQuery(id+"F3.wireOp",EDGE,"E11.6.left");var subQ2=makeQuery(id+"F3.imprint","INTERSECT",VERTEX,{"derivedFrom":[subQ1,subQ0]});Q95=makeQuery(id+"F3.imprint","IMPRINT",FACE,{"disambiguationData":[TD([[makeQuery(id+"F3.imprint","IMPRINT",EDGE,{"disambiguationData":[TD([[subQ2,-1.0]])],"derivedFrom":subQ1}),-1.0]])]});}
            var Q96;
            {var subQ0=sQuery(id+"F3.wireOp",EDGE,"E11.9.right");var subQ1=sQuery(id+"F3.wireOp",EDGE,"E11.6.left");var subQ2=makeQuery(id+"F3.imprint","INTERSECT",VERTEX,{"derivedFrom":[subQ1,subQ0]});Q96=makeQuery(id+"F3.imprint","IMPRINT",FACE,{"disambiguationData":[TD([[makeQuery(id+"F3.imprint","IMPRINT",EDGE,{"disambiguationData":[TD([[subQ2,-1.0]])],"derivedFrom":subQ1}),-1.0]])]});}
            var Q97;
            {var subQ0=sQuery(id+"F3.wireOp",EDGE,"E11.6.left");var subQ1=sQuery(id+"F3.wireOp",EDGE,"E11.4.left");var subQ2=makeQuery(id+"F3.imprint","INTERSECT",VERTEX,{"derivedFrom":[subQ1,subQ0]});Q97=makeQuery(id+"F3.imprint","IMPRINT",FACE,{"disambiguationData":[TD([[makeQuery(id+"F3.imprint","IMPRINT",EDGE,{"disambiguationData":[TD([[subQ2,-1.0]])],"derivedFrom":subQ1}),-1.0]])]});}
            var Q98;
            {var subQ0=sQuery(id+"F3.wireOp",EDGE,"E11.6.left");var subQ1=sQuery(id+"F3.wireOp",EDGE,"E11.1.left");var subQ2=makeQuery(id+"F3.imprint","INTERSECT",VERTEX,{"derivedFrom":[subQ1,subQ0]});Q98=makeQuery(id+"F3.imprint","IMPRINT",FACE,{"disambiguationData":[TD([[makeQuery(id+"F3.imprint","IMPRINT",EDGE,{"disambiguationData":[TD([[subQ2,-1.0]])],"derivedFrom":subQ1}),-1.0]])]});}
            var Q99;
            {var subQ0=sQuery(id+"F3.wireOp",EDGE,"E11.11.left");var subQ1=sQuery(id+"F3.wireOp",EDGE,"E11.1.left");var subQ2=makeQuery(id+"F3.imprint","INTERSECT",VERTEX,{"derivedFrom":[subQ1,subQ0]});Q99=makeQuery(id+"F3.imprint","IMPRINT",FACE,{"disambiguationData":[TD([[makeQuery(id+"F3.imprint","IMPRINT",EDGE,{"disambiguationData":[TD([[subQ2,-1.0]])],"derivedFrom":subQ1}),-1.0]])]});}
            var Q100;
            {var subQ0=sQuery(id+"F3.wireOp",EDGE,"E11.11.left");var subQ1=sQuery(id+"F3.wireOp",EDGE,"E11.1.right");var subQ2=makeQuery(id+"F3.imprint","INTERSECT",VERTEX,{"derivedFrom":[subQ1,subQ0]});Q100=makeQuery(id+"F3.imprint","IMPRINT",FACE,{"disambiguationData":[TD([[makeQuery(id+"F3.imprint","IMPRINT",EDGE,{"disambiguationData":[TD([[subQ2,-1.0]])],"derivedFrom":subQ1}),-1.0]])]});}
            var Q101;
            {var subQ0=sQuery(id+"F3.wireOp",EDGE,"E11.11.left");var subQ1=sQuery(id+"F3.wireOp",EDGE,"E11.4.left");var subQ2=makeQuery(id+"F3.imprint","INTERSECT",VERTEX,{"derivedFrom":[subQ1,subQ0]});Q101=makeQuery(id+"F3.imprint","IMPRINT",FACE,{"disambiguationData":[TD([[makeQuery(id+"F3.imprint","IMPRINT",EDGE,{"disambiguationData":[TD([[subQ2,-1.0]])],"derivedFrom":subQ1}),-1.0]])]});}
            var Q102;
            {var subQ0=sQuery(id+"F3.wireOp",EDGE,"E11.11.left");var subQ1=sQuery(id+"F3.wireOp",EDGE,"E11.9.right");var subQ2=makeQuery(id+"F3.imprint","INTERSECT",VERTEX,{"derivedFrom":[subQ1,subQ0]});Q102=makeQuery(id+"F3.imprint","IMPRINT",FACE,{"disambiguationData":[TD([[makeQuery(id+"F3.imprint","IMPRINT",EDGE,{"disambiguationData":[TD([[subQ2,-1.0]])],"derivedFrom":subQ1}),-1.0]])]});}
            var Q103;
            {var subQ0=sQuery(id+"F3.wireOp",EDGE,"E11.11.left");var subQ1=sQuery(id+"F3.wireOp",EDGE,"E11.10.left");var subQ2=makeQuery(id+"F3.imprint","INTERSECT",VERTEX,{"derivedFrom":[subQ1,subQ0]});Q103=makeQuery(id+"F3.imprint","IMPRINT",FACE,{"disambiguationData":[TD([[makeQuery(id+"F3.imprint","IMPRINT",EDGE,{"disambiguationData":[TD([[subQ2,-1.0]])],"derivedFrom":subQ1}),-1.0]])]});}
            var Q104;
            {var subQ0=sQuery(id+"F3.wireOp",EDGE,"E11.11.left");var subQ1=sQuery(id+"F3.wireOp",EDGE,"E11.9.left");var subQ2=makeQuery(id+"F3.imprint","INTERSECT",VERTEX,{"derivedFrom":[subQ1,subQ0]});Q104=makeQuery(id+"F3.imprint","IMPRINT",FACE,{"disambiguationData":[TD([[makeQuery(id+"F3.imprint","IMPRINT",EDGE,{"disambiguationData":[TD([[subQ2,-1.0]])],"derivedFrom":subQ1}),-1.0]])]});}
            var Q105;
            {var subQ0=sQuery(id+"F3.wireOp",EDGE,"E11.11.left");var subQ1=sQuery(id+"F3.wireOp",EDGE,"E11.2.left");var subQ2=makeQuery(id+"F3.imprint","INTERSECT",VERTEX,{"derivedFrom":[subQ1,subQ0]});Q105=makeQuery(id+"F3.imprint","IMPRINT",FACE,{"disambiguationData":[TD([[makeQuery(id+"F3.imprint","IMPRINT",EDGE,{"disambiguationData":[TD([[subQ2,-1.0]])],"derivedFrom":subQ1}),-1.0]])]});}
            var Q106;
            {var subQ0=sQuery(id+"F3.wireOp",EDGE,"E11.11.left");var subQ1=sQuery(id+"F3.wireOp",EDGE,"E11.2.left");var subQ2=makeQuery(id+"F3.imprint","INTERSECT",VERTEX,{"derivedFrom":[subQ1,subQ0]});Q106=makeQuery(id+"F3.imprint","IMPRINT",FACE,{"disambiguationData":[TD([[makeQuery(id+"F3.imprint","IMPRINT",EDGE,{"disambiguationData":[TD([[subQ2,-1.0]])],"derivedFrom":subQ1}),1.0]])]});}
            var Q107;
            {var subQ0=sQuery(id+"F3.wireOp",EDGE,"E11.11.left");var subQ1=sQuery(id+"F3.wireOp",EDGE,"E11.2.right");var subQ2=makeQuery(id+"F3.imprint","INTERSECT",VERTEX,{"derivedFrom":[subQ1,subQ0]});Q107=makeQuery(id+"F3.imprint","IMPRINT",FACE,{"disambiguationData":[TD([[makeQuery(id+"F3.imprint","IMPRINT",EDGE,{"disambiguationData":[TD([[subQ2,-1.0]])],"derivedFrom":subQ1}),-1.0]])]});}
            var Q108;
            {var subQ0=sQuery(id+"F3.wireOp",EDGE,"E11.11.left");var subQ1=sQuery(id+"F3.wireOp",EDGE,"E11.3.right");var subQ2=makeQuery(id+"F3.imprint","INTERSECT",VERTEX,{"derivedFrom":[subQ1,subQ0]});Q108=makeQuery(id+"F3.imprint","IMPRINT",FACE,{"disambiguationData":[TD([[makeQuery(id+"F3.imprint","IMPRINT",EDGE,{"disambiguationData":[TD([[subQ2,-1.0]])],"derivedFrom":subQ1}),-1.0]])]});}
            var Q109;
            {var subQ0=sQuery(id+"F3.wireOp",EDGE,"E11.11.left");var subQ1=sQuery(id+"F3.wireOp",EDGE,"E11.3.left");var subQ2=makeQuery(id+"F3.imprint","INTERSECT",VERTEX,{"derivedFrom":[subQ1,subQ0]});Q109=makeQuery(id+"F3.imprint","IMPRINT",FACE,{"disambiguationData":[TD([[makeQuery(id+"F3.imprint","IMPRINT",EDGE,{"disambiguationData":[TD([[subQ2,-1.0]])],"derivedFrom":subQ1}),-1.0]])]});}
            var Q110;
            {var subQ0=sQuery(id+"F3.wireOp",EDGE,"E11.6.right");var subQ1=sQuery(id+"F3.wireOp",EDGE,"E11.2.left");var subQ2=makeQuery(id+"F3.imprint","INTERSECT",VERTEX,{"derivedFrom":[subQ1,subQ0]});Q110=makeQuery(id+"F3.imprint","IMPRINT",FACE,{"disambiguationData":[TD([[makeQuery(id+"F3.imprint","IMPRINT",EDGE,{"disambiguationData":[TD([[subQ2,-1.0]])],"derivedFrom":subQ1}),-1.0]])]});}
            var Q111;
            {var subQ0=sQuery(id+"F3.wireOp",EDGE,"E11.6.left");var subQ1=sQuery(id+"F3.wireOp",EDGE,"E11.2.left");var subQ2=makeQuery(id+"F3.imprint","INTERSECT",VERTEX,{"derivedFrom":[subQ1,subQ0]});Q111=makeQuery(id+"F3.imprint","IMPRINT",FACE,{"disambiguationData":[TD([[makeQuery(id+"F3.imprint","IMPRINT",EDGE,{"disambiguationData":[TD([[subQ2,-1.0]])],"derivedFrom":subQ1}),1.0]])]});}
            var Q112;
            {var subQ0=sQuery(id+"F3.wireOp",EDGE,"E11.10.right");var subQ1=sQuery(id+"F3.wireOp",EDGE,"E11.0.right");var subQ2=makeQuery(id+"F3.imprint","INTERSECT",VERTEX,{"derivedFrom":[subQ1,subQ0]});Q112=makeQuery(id+"F3.imprint","IMPRINT",FACE,{"disambiguationData":[TD([[makeQuery(id+"F3.imprint","IMPRINT",EDGE,{"disambiguationData":[TD([[subQ2,-1.0]])],"derivedFrom":subQ1}),-1.0]])]});}
            var Q113;
            {var subQ0=sQuery(id+"F3.wireOp",EDGE,"E11.10.left");var subQ1=sQuery(id+"F3.wireOp",EDGE,"E11.6.left");var subQ2=makeQuery(id+"F3.imprint","INTERSECT",VERTEX,{"derivedFrom":[subQ1,subQ0]});Q113=makeQuery(id+"F3.imprint","IMPRINT",FACE,{"disambiguationData":[TD([[makeQuery(id+"F3.imprint","IMPRINT",EDGE,{"disambiguationData":[TD([[subQ2,-1.0]])],"derivedFrom":subQ1}),-1.0]])]});}
            var Q114;
            {var subQ0=sQuery(id+"F3.wireOp",EDGE,"E11.9.right");var subQ1=sQuery(id+"F3.wireOp",EDGE,"E11.0.right");var subQ2=makeQuery(id+"F3.imprint","INTERSECT",VERTEX,{"derivedFrom":[subQ1,subQ0]});Q114=makeQuery(id+"F3.imprint","IMPRINT",FACE,{"disambiguationData":[TD([[makeQuery(id+"F3.imprint","IMPRINT",EDGE,{"disambiguationData":[TD([[subQ2,-1.0]])],"derivedFrom":subQ1}),-1.0]])]});}
            var Q115;
            {var subQ0=sQuery(id+"F3.wireOp",EDGE,"E11.6.left");var subQ1=sQuery(id+"F3.wireOp",EDGE,"E11.4.right");var subQ2=makeQuery(id+"F3.imprint","INTERSECT",VERTEX,{"derivedFrom":[subQ1,subQ0]});Q115=makeQuery(id+"F3.imprint","IMPRINT",FACE,{"disambiguationData":[TD([[makeQuery(id+"F3.imprint","IMPRINT",EDGE,{"disambiguationData":[TD([[subQ2,-1.0]])],"derivedFrom":subQ1}),-1.0]])]});}
            var Q116;
            {var subQ0=sQuery(id+"F3.wireOp",EDGE,"E11.4.right");var subQ1=sQuery(id+"F3.wireOp",EDGE,"E11.0.right");var subQ2=makeQuery(id+"F3.imprint","INTERSECT",VERTEX,{"derivedFrom":[subQ1,subQ0]});Q116=makeQuery(id+"F3.imprint","IMPRINT",FACE,{"disambiguationData":[TD([[makeQuery(id+"F3.imprint","IMPRINT",EDGE,{"disambiguationData":[TD([[subQ2,-1.0]])],"derivedFrom":subQ1}),-1.0]])]});}
            var Q117;
            {var subQ0=sQuery(id+"F3.wireOp",EDGE,"E11.6.left");var subQ1=sQuery(id+"F3.wireOp",EDGE,"E11.1.right");var subQ2=makeQuery(id+"F3.imprint","INTERSECT",VERTEX,{"derivedFrom":[subQ1,subQ0]});Q117=makeQuery(id+"F3.imprint","IMPRINT",FACE,{"disambiguationData":[TD([[makeQuery(id+"F3.imprint","IMPRINT",EDGE,{"disambiguationData":[TD([[subQ2,-1.0]])],"derivedFrom":subQ1}),-1.0]])]});}
            var Q118;
            {var subQ0=sQuery(id+"F3.wireOp",EDGE,"E11.1.right");var subQ1=sQuery(id+"F3.wireOp",EDGE,"E11.0.right");var subQ2=makeQuery(id+"F3.imprint","INTERSECT",VERTEX,{"derivedFrom":[subQ1,subQ0]});Q118=makeQuery(id+"F3.imprint","IMPRINT",FACE,{"disambiguationData":[TD([[makeQuery(id+"F3.imprint","IMPRINT",EDGE,{"disambiguationData":[TD([[subQ2,-1.0]])],"derivedFrom":subQ1}),-1.0]])]});}
            var Q119;
            {var subQ0=sQuery(id+"F3.wireOp",EDGE,"E11.6.left");var subQ1=sQuery(id+"F3.wireOp",EDGE,"E11.1.left");var subQ2=makeQuery(id+"F3.imprint","INTERSECT",VERTEX,{"derivedFrom":[subQ1,subQ0]});Q119=makeQuery(id+"F3.imprint","IMPRINT",FACE,{"disambiguationData":[TD([[makeQuery(id+"F3.imprint","IMPRINT",EDGE,{"disambiguationData":[TD([[subQ2,-1.0]])],"derivedFrom":subQ1}),1.0]])]});}
            var Q120;
            {var subQ0=sQuery(id+"F3.wireOp",EDGE,"E11.6.right");var subQ1=sQuery(id+"F3.wireOp",EDGE,"E11.1.left");var subQ2=makeQuery(id+"F3.imprint","INTERSECT",VERTEX,{"derivedFrom":[subQ1,subQ0]});Q120=makeQuery(id+"F3.imprint","IMPRINT",FACE,{"disambiguationData":[TD([[makeQuery(id+"F3.imprint","IMPRINT",EDGE,{"disambiguationData":[TD([[subQ2,-1.0]])],"derivedFrom":subQ1}),-1.0]])]});}
            var Q121;
            {var subQ0=sQuery(id+"F3.wireOp",EDGE,"E11.6.right");var subQ1=sQuery(id+"F3.wireOp",EDGE,"E11.4.left");var subQ2=makeQuery(id+"F3.imprint","INTERSECT",VERTEX,{"derivedFrom":[subQ1,subQ0]});Q121=makeQuery(id+"F3.imprint","IMPRINT",FACE,{"disambiguationData":[TD([[makeQuery(id+"F3.imprint","IMPRINT",EDGE,{"disambiguationData":[TD([[subQ2,-1.0]])],"derivedFrom":subQ1}),-1.0]])]});}
            var Q122;
            {var subQ0=sQuery(id+"F3.wireOp",EDGE,"E11.9.right");var subQ1=sQuery(id+"F3.wireOp",EDGE,"E11.6.right");var subQ2=makeQuery(id+"F3.imprint","INTERSECT",VERTEX,{"derivedFrom":[subQ1,subQ0]});Q122=makeQuery(id+"F3.imprint","IMPRINT",FACE,{"disambiguationData":[TD([[makeQuery(id+"F3.imprint","IMPRINT",EDGE,{"disambiguationData":[TD([[subQ2,-1.0]])],"derivedFrom":subQ1}),-1.0]])]});}
            var Q123;
            {var subQ0=sQuery(id+"F3.wireOp",EDGE,"E11.11.left");var subQ1=sQuery(id+"F3.wireOp",EDGE,"E11.4.right");var subQ2=makeQuery(id+"F3.imprint","INTERSECT",VERTEX,{"derivedFrom":[subQ1,subQ0]});Q123=makeQuery(id+"F3.imprint","IMPRINT",FACE,{"disambiguationData":[TD([[makeQuery(id+"F3.imprint","IMPRINT",EDGE,{"disambiguationData":[TD([[subQ2,-1.0]])],"derivedFrom":subQ1}),-1.0]])]});}
            var Q124;
            {var subQ0=sQuery(id+"F3.wireOp",EDGE,"E11.11.left");var subQ1=sQuery(id+"F3.wireOp",EDGE,"E11.1.left");var subQ2=makeQuery(id+"F3.imprint","INTERSECT",VERTEX,{"derivedFrom":[subQ1,subQ0]});Q124=makeQuery(id+"F3.imprint","IMPRINT",FACE,{"disambiguationData":[TD([[makeQuery(id+"F3.imprint","IMPRINT",EDGE,{"disambiguationData":[TD([[subQ2,-1.0]])],"derivedFrom":subQ1}),1.0]])]});}
            var Q125;
            {var subQ0=sQuery(id+"F3.wireOp",EDGE,"E11.11.right");var subQ1=sQuery(id+"F3.wireOp",EDGE,"E11.1.left");var subQ2=makeQuery(id+"F3.imprint","INTERSECT",VERTEX,{"derivedFrom":[subQ1,subQ0]});Q125=makeQuery(id+"F3.imprint","IMPRINT",FACE,{"disambiguationData":[TD([[makeQuery(id+"F3.imprint","IMPRINT",EDGE,{"disambiguationData":[TD([[subQ2,-1.0]])],"derivedFrom":subQ1}),-1.0]])]});}
            var Q126;
            {var subQ0=sQuery(id+"F3.wireOp",EDGE,"E11.11.right");var subQ1=sQuery(id+"F3.wireOp",EDGE,"E11.4.left");var subQ2=makeQuery(id+"F3.imprint","INTERSECT",VERTEX,{"derivedFrom":[subQ1,subQ0]});Q126=makeQuery(id+"F3.imprint","IMPRINT",FACE,{"disambiguationData":[TD([[makeQuery(id+"F3.imprint","IMPRINT",EDGE,{"disambiguationData":[TD([[subQ2,-1.0]])],"derivedFrom":subQ1}),-1.0]])]});}
            var Q127;
            {var subQ0=sQuery(id+"F3.wireOp",EDGE,"E11.9.right");var subQ1=sQuery(id+"F3.wireOp",EDGE,"E11.5.left");var subQ2=makeQuery(id+"F3.imprint","INTERSECT",VERTEX,{"derivedFrom":[subQ1,subQ0]});Q127=makeQuery(id+"F3.imprint","IMPRINT",FACE,{"disambiguationData":[TD([[makeQuery(id+"F3.imprint","IMPRINT",EDGE,{"disambiguationData":[TD([[subQ2,-1.0]])],"derivedFrom":subQ1}),1.0]])]});}
            var Q128;
            {var subQ0=sQuery(id+"F3.wireOp",EDGE,"E11.10.right");var subQ1=sQuery(id+"F3.wireOp",EDGE,"E11.5.left");var subQ2=makeQuery(id+"F3.imprint","INTERSECT",VERTEX,{"derivedFrom":[subQ1,subQ0]});Q128=makeQuery(id+"F3.imprint","IMPRINT",FACE,{"disambiguationData":[TD([[makeQuery(id+"F3.imprint","IMPRINT",EDGE,{"disambiguationData":[TD([[subQ2,-1.0]])],"derivedFrom":subQ1}),1.0]])]});}
            var Q129;
            {var subQ0=sQuery(id+"F3.wireOp",EDGE,"E11.10.right");var subQ1=sQuery(id+"F3.wireOp",EDGE,"E11.6.right");var subQ2=makeQuery(id+"F3.imprint","INTERSECT",VERTEX,{"derivedFrom":[subQ1,subQ0]});Q129=makeQuery(id+"F3.imprint","IMPRINT",FACE,{"disambiguationData":[TD([[makeQuery(id+"F3.imprint","IMPRINT",EDGE,{"disambiguationData":[TD([[subQ2,-1.0]])],"derivedFrom":subQ1}),-1.0]])]});}
            var Q130;
            {var subQ0=sQuery(id+"F3.wireOp",EDGE,"E11.11.right");var subQ1=sQuery(id+"F3.wireOp",EDGE,"E11.2.left");var subQ2=makeQuery(id+"F3.imprint","INTERSECT",VERTEX,{"derivedFrom":[subQ1,subQ0]});Q130=makeQuery(id+"F3.imprint","IMPRINT",FACE,{"disambiguationData":[TD([[makeQuery(id+"F3.imprint","IMPRINT",EDGE,{"disambiguationData":[TD([[subQ2,-1.0]])],"derivedFrom":subQ1}),-1.0]])]});}
            var Q131;
            {var subQ0=sQuery(id+"F3.wireOp",EDGE,"E11.11.right");var subQ1=sQuery(id+"F3.wireOp",EDGE,"E11.3.left");var subQ2=makeQuery(id+"F3.imprint","INTERSECT",VERTEX,{"derivedFrom":[subQ1,subQ0]});Q131=makeQuery(id+"F3.imprint","IMPRINT",FACE,{"disambiguationData":[TD([[makeQuery(id+"F3.imprint","IMPRINT",EDGE,{"disambiguationData":[TD([[subQ2,-1.0]])],"derivedFrom":subQ1}),-1.0]])]});}
            var Q132;
            Q132=makeQuery(id+"F1.opExtrude","CAP_FACE",FACE,{"disambiguationData":[OSD([sQuery(id+"F0.wireOp",EDGE,"E0.bottom"),sQuery(id+"F0.wireOp",EDGE,"E0.top"),sQuery(id+"F0.wireOp",EDGE,"E0.left"),sQuery(id+"F0.wireOp",EDGE,"E0.right")])],"isStart":false});
            extrude(context, id + "F4", {"entities" : qUnion([Q0, Q1, Q2, Q3, Q4, Q5, Q6, Q7, Q8, Q9, Q10, Q11, Q12, Q13, Q14, Q15, Q16, Q17, Q18, Q19, Q20, Q21, Q22, Q23, Q24, Q25, Q26, Q27, Q28, Q29, Q30, Q31, Q32, Q33, Q34, Q35, Q36, Q37, Q38, Q39, Q40, Q41, Q42, Q43, Q44, Q45, Q46, Q47, Q48, Q49, Q50, Q51, Q52, Q53, Q54, Q55, Q56, Q57, Q58, Q59, Q60, Q61, Q62, Q63, Q64, Q65, Q66, Q67, Q68, Q69, Q70, Q71, Q72, Q73, Q74, Q75, Q76, Q77, Q78, Q79, Q80, Q81, Q82, Q83, Q84, Q85, Q86, Q87, Q88, Q89, Q90, Q91, Q92, Q93, Q94, Q95, Q96, Q97, Q98, Q99, Q100, Q101, Q102, Q103, Q104, Q105, Q106, Q107, Q108, Q109, Q110, Q111, Q112, Q113, Q114, Q115, Q116, Q117, Q118, Q119, Q120, Q121, Q122, Q123, Q124, Q125, Q126, Q127, Q128, Q129, Q130, Q131]), "operationType" : NewBodyOperationType.ADD, "endBound" : BoundingType.UP_TO_SURFACE, "depth" : 13 * mm, "endBoundEntityFace" : qUnion([Q132]), "offsetDistance" : 25 * mm});
        }
        {
            var Q0;
            Q0=makeQuery(id+"F1.opExtrude","SWEPT_FACE",FACE,{"disambiguationData":[OSD([sQuery(id+"F0.wireOp",EDGE,"E0.left")])]});
            var sketch = newSketch(context, id + "F5", { "sketchPlane" : qUnion([Q0])});
            skCircle(sketch, "E12", {"center": v(80.7, 11.7) * mm, "radius": 2 * mm});
            skCircle(sketch, "E13.0", {"center": v(80.7, 11.7) * mm, "radius": 1 * mm});
            skLineSegment(sketch, "E14", {"start": v(80.7, 11.7) * mm, "end": v(80, 11) * mm, "construction": true});
            skLineSegment(sketch, "E15", {"start": v(80.7, 11.7) * mm, "end": v(80.7, 10.7) * mm, "construction": true});
            skSolve(sketch);
        }
        {
            var Q0;
            {var subQ6=sQuery(id+"F5.wireOp",EDGE,"E13.0");Q0=makeQuery(id+"F5.imprint","IMPRINT",FACE,{"disambiguationData":[TD([[makeQuery(id+"F5.imprint","IMPRINT",EDGE,{"derivedFrom":subQ6}),-1.0]])]});}
            var Q1;
            {var subQ0=sQuery(id+"F5.wireOp",EDGE,"E12");var subQ1=sQuery(id+"F0.wireOp",EDGE,"E0.left");var subQ4=makeQuery(id+"F1.opExtrude","CAP_EDGE",EDGE,{"disambiguationData":[OSD([subQ1])],"isStart":false});var subQ5=makeQuery(id+"F5.imprint","INTERSECT",VERTEX,{"derivedFrom":[subQ4,subQ0]});Q1=makeQuery(id+"F5.imprint","IMPRINT",FACE,{"disambiguationData":[TD([[makeQuery(id+"F5.imprint","IMPRINT",EDGE,{"disambiguationData":[TD([[subQ5,-1.0]])],"derivedFrom":subQ0}),1.0]])]});}
            var Q2;
            Q2=makeQuery(id+"F1.opExtrude","SWEPT_FACE",FACE,{"disambiguationData":[OSD([sQuery(id+"F0.wireOp",EDGE,"E0.right")])]});
            extrude(context, id + "F6", {"entities" : qUnion([Q0, Q1]), "operationType" : NewBodyOperationType.ADD, "oppositeDirection" : true, "depth" : 25 * mm, "endBoundEntityFace" : qUnion([Q2]), "offsetDistance" : 25 * mm});
        }
        {
            var Q0;
            {var subQ0=sQuery(id+"F0.wireOp",EDGE,"E0.left");var subQ1=makeQuery(id+"F1.opExtrude","CAP_EDGE",EDGE,{"disambiguationData":[OSD([subQ0])],"isStart":true});Q0=makeQuery(id+"F5.imprint","IMPRINT",FACE,{"disambiguationData":[TD([[makeQuery(id+"F5.imprint","IMPRINT",EDGE,{"derivedFrom":subQ1}),1.0]])]});}
            var Q1;
            Q1=makeQuery(id+"F1.opExtrude","SWEPT_FACE",FACE,{"disambiguationData":[OSD([sQuery(id+"F0.wireOp",EDGE,"E0.right")])]});
            cPlane(context, id + "F7", {"entities" : qUnion([Q0, Q1]), "cplaneType" : CPlaneType.MID_PLANE, "offset" : 25 * mm, "width" : 150 * mm, "height" : 150 * mm});
        }
        {
            var Q0;
            Q0=qCreatedBy(id+"F7.planeOp",FACE);
            var sketch = newSketch(context, id + "F8", { "sketchPlane" : qUnion([Q0])});
            skCircle(sketch, "E16.0", {"center": v(80.7, 11.7) * mm, "radius": 2 * mm});
            skCircle(sketch, "E17.0", {"center": v(80.7, 11.7) * mm, "radius": 1 * mm});
            skSolve(sketch);
        }
        {
            var Q0;
            Q0=makeQuery(id+"F8.imprint","IMPRINT",FACE,{"disambiguationData":[TD([[makeQuery(id+"F8.imprint","IMPRINT",EDGE,{"derivedFrom":sQuery(id+"F8.wireOp",EDGE,"E16.0")}),1.0]])]});
            extrude(context, id + "F9", {"entities" : qUnion([Q0]), "operationType" : NewBodyOperationType.ADD, "endBound" : BoundingType.SYMMETRIC, "depth" : 25 * mm, "offsetDistance" : 25 * mm});
        }
        {
            var Q0;
            Q0=qCreatedBy(id+"F7.planeOp",FACE);
            var sketch = newSketch(context, id + "F10", { "sketchPlane" : qUnion([Q0])});
            skPoint(sketch, "E18.0", {"position": v(0, 11) * mm});
            skLineSegment(sketch, "E19.bottom", {"start": v(0, 10) * mm, "end": v(1, 10) * mm});
            skLineSegment(sketch, "E19.top", {"start": v(0, 8) * mm, "end": v(1, 8) * mm});
            skLineSegment(sketch, "E19.left", {"start": v(0, 10) * mm, "end": v(0, 8) * mm});
            skLineSegment(sketch, "E19.right", {"start": v(1, 10) * mm, "end": v(1, 8) * mm});
            skSolve(sketch);
        }
        {
            var Q0;
            Q0 = qSketchRegion(id + "F10", true);
            extrude(context, id + "F11", {"entities" : qUnion([Q0]), "operationType" : NewBodyOperationType.REMOVE, "endBound" : BoundingType.SYMMETRIC, "depth" : 5 * mm, "offsetDistance" : 25 * mm});
        }
        {
            var Q0;
            Q0=makeQuery(id+"F1.opExtrude","SWEPT_EDGE",EDGE,{"disambiguationData":[OSD([sQuery(id+"F0.wireOp",EDGE,"E0.bottom"),sQuery(id+"F0.wireOp",EDGE,"E0.left")])]});
            var Q1;
            Q1=makeQuery(id+"F1.opExtrude","SWEPT_EDGE",EDGE,{"disambiguationData":[OSD([sQuery(id+"F0.wireOp",EDGE,"E0.bottom"),sQuery(id+"F0.wireOp",EDGE,"E0.right")])]});
            fillet(context, id + "F12", {"entities" : qUnion([Q0, Q1]), "radius" : 3 * mm, "tangentPropagation" : true, "allowEdgeOverflow" : false});
        }
    });
